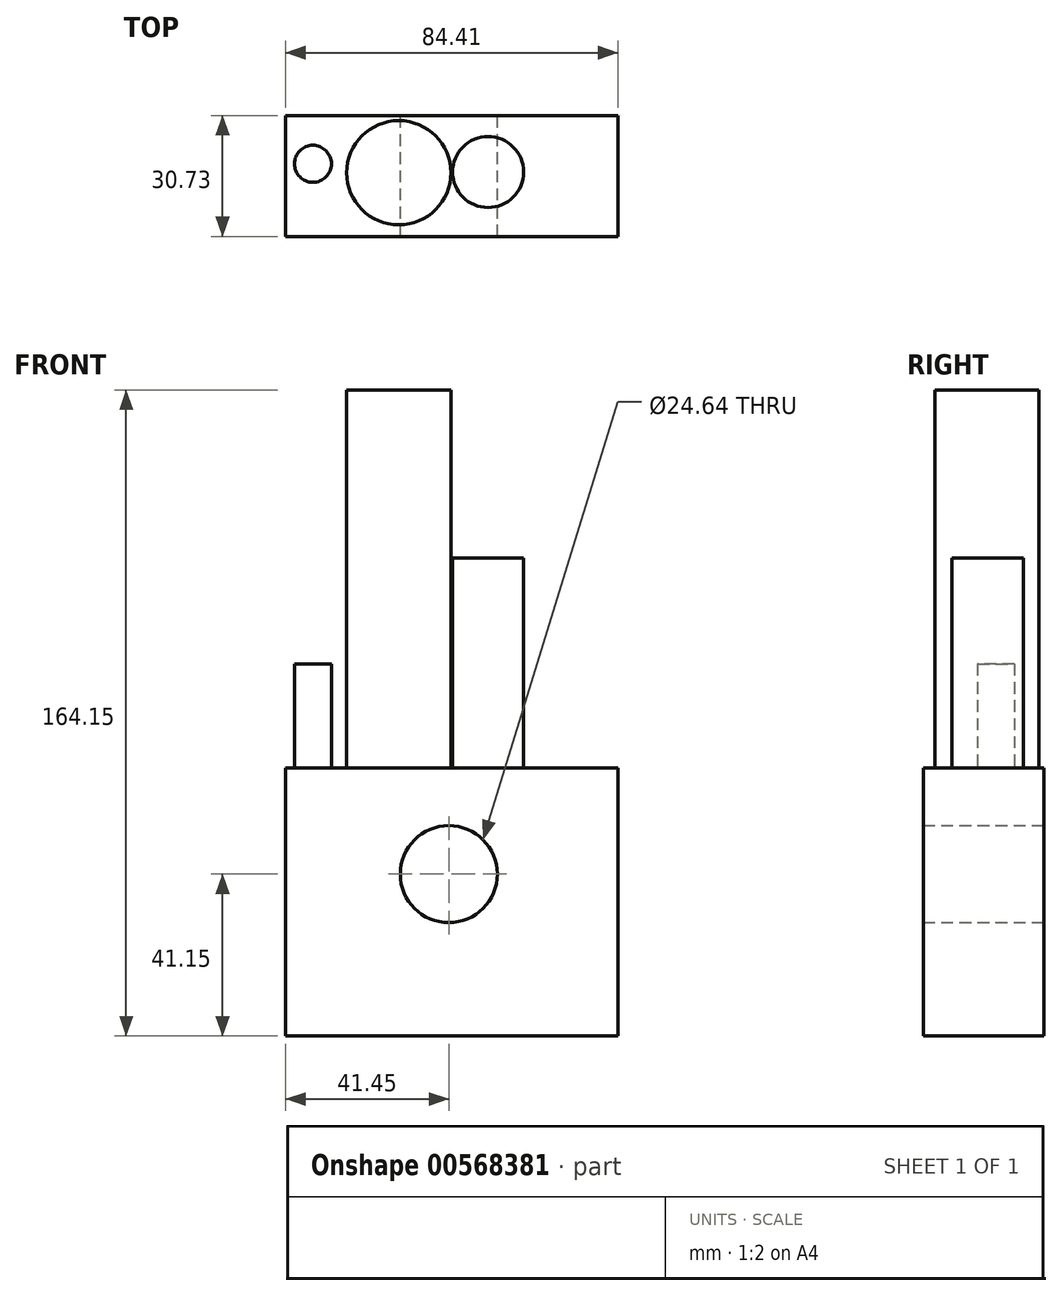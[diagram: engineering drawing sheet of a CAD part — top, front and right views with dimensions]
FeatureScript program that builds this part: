
annotation { "Feature Type Name" : "Feature", "Feature Type Description" : "" }
export const myFeature = defineFeature(function(context is Context, id is Id, definition is map)
    precondition{}
    {
        {
            var Q0;
            Q0=qCreatedBy(makeId("Front.planeOp"),FACE);
            var sketch = newSketch(context, id + "F0", { "sketchPlane" : qUnion([Q0])});
            skLineSegment(sketch, "E0.bottom", {"start": v(-41.45, 27) * mm, "end": v(42.96, 27) * mm});
            skLineSegment(sketch, "E0.top", {"start": v(-41.45, -41.15) * mm, "end": v(42.96, -41.15) * mm});
            skLineSegment(sketch, "E0.left", {"start": v(-41.45, 27) * mm, "end": v(-41.45, -41.15) * mm});
            skLineSegment(sketch, "E0.right", {"start": v(42.96, 27) * mm, "end": v(42.96, -41.15) * mm});
            skCircle(sketch, "E1", {"center": v(0, 0) * mm, "radius": 12.32 * mm});
            skSolve(sketch);
        }
        {
            var Q0;
            Q0=makeQuery(id+"F0.imprint","IMPRINT",FACE,{"disambiguationData":[TD([[makeQuery(id+"F0.imprint","IMPRINT",EDGE,{"derivedFrom":sQuery(id+"F0.wireOp",EDGE,"E0.bottom")}),-1.0]])]});
            extrude(context, id + "F1", {"entities" : qUnion([Q0]), "depth" : 30.73 * mm, "offsetDistance" : 25.4 * mm});
        }
        {
            var Q0;
            Q0=makeQuery(id+"F1.opExtrude","SWEPT_FACE",FACE,{"disambiguationData":[OSD([sQuery(id+"F0.wireOp",EDGE,"E0.bottom")])]});
            var sketch = newSketch(context, id + "F2", { "sketchPlane" : qUnion([Q0])});
            skCircle(sketch, "E2", {"center": v(-12.7, -14.53) * mm, "radius": 13.24 * mm});
            skCircle(sketch, "E3", {"center": v(9.99, -14.35) * mm, "radius": 9.02 * mm});
            skCircle(sketch, "E4", {"center": v(-34.52, -12.26) * mm, "radius": 4.7 * mm});
            skSolve(sketch);
        }
        {
            var Q0;
            Q0=makeQuery(id+"F2.imprint","IMPRINT",FACE,{"disambiguationData":[TD([[makeQuery(id+"F2.imprint","IMPRINT",EDGE,{"derivedFrom":sQuery(id+"F2.wireOp",EDGE,"E2")}),1.0]])]});
            extrude(context, id + "F3", {"entities" : qUnion([Q0]), "operationType" : NewBodyOperationType.ADD, "depth" : 96.01 * mm, "offsetDistance" : 25.4 * mm});
        }
        {
            var Q0;
            Q0=makeQuery(id+"F2.imprint","IMPRINT",FACE,{"disambiguationData":[TD([[makeQuery(id+"F2.imprint","IMPRINT",EDGE,{"derivedFrom":sQuery(id+"F2.wireOp",EDGE,"E3")}),1.0]])]});
            extrude(context, id + "F4", {"entities" : qUnion([Q0]), "operationType" : NewBodyOperationType.ADD, "depth" : 53.34 * mm, "offsetDistance" : 25.4 * mm});
        }
        {
            var Q0;
            Q0=makeQuery(id+"F2.imprint","IMPRINT",FACE,{"disambiguationData":[TD([[makeQuery(id+"F2.imprint","IMPRINT",EDGE,{"derivedFrom":sQuery(id+"F2.wireOp",EDGE,"E4")}),1.0]])]});
            extrude(context, id + "F5", {"entities" : qUnion([Q0]), "operationType" : NewBodyOperationType.ADD, "depth" : 26.42 * mm, "offsetDistance" : 25.4 * mm});
        }
    });
